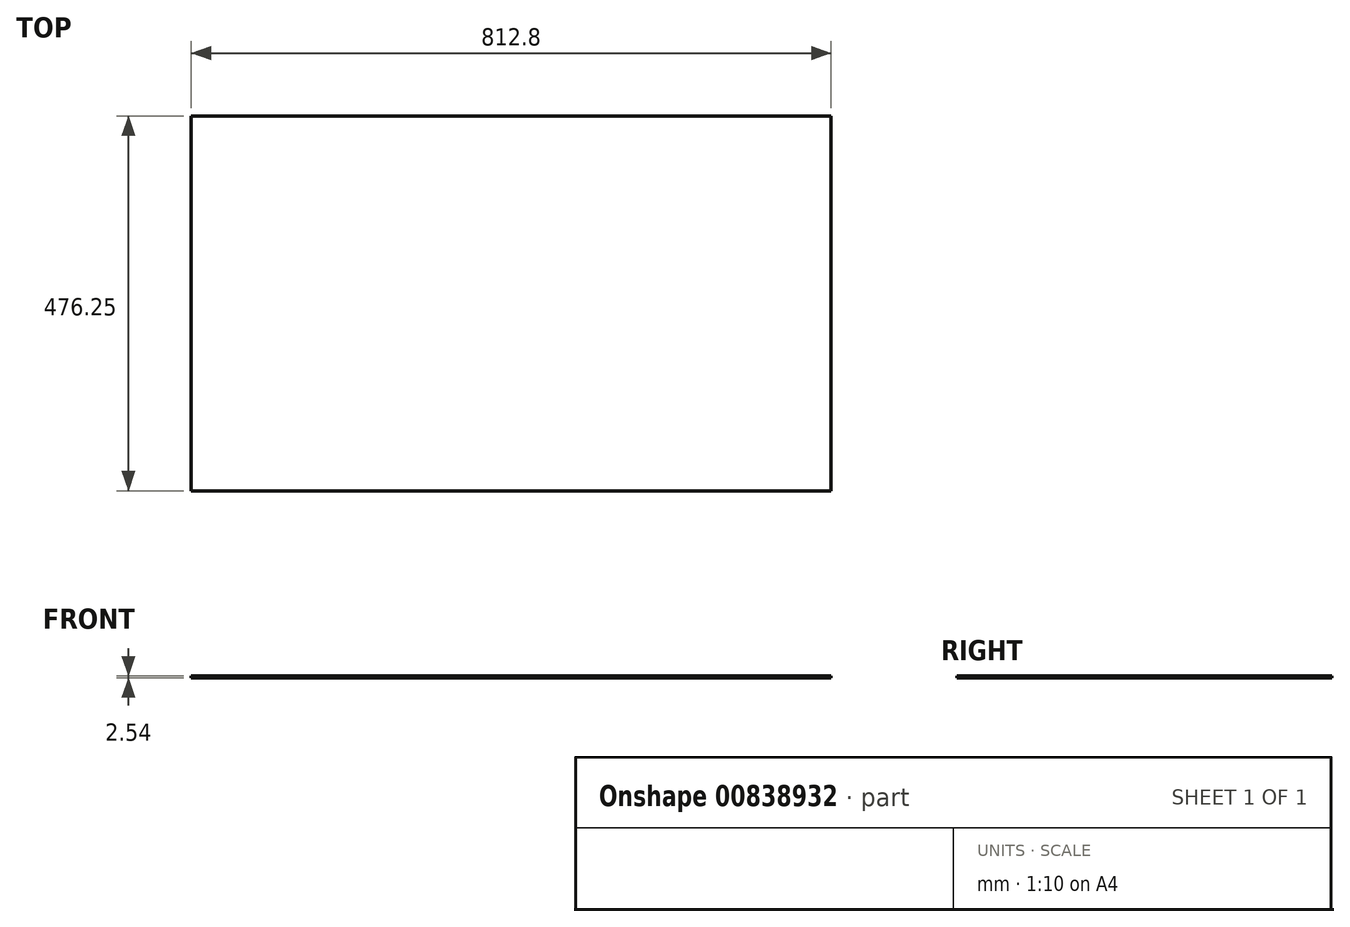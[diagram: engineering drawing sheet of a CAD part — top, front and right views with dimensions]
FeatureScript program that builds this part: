
annotation { "Feature Type Name" : "Feature", "Feature Type Description" : "" }
export const myFeature = defineFeature(function(context is Context, id is Id, definition is map)
    precondition{}
    {
        {
            var Q0;
            Q0=qCreatedBy(makeId("Top.planeOp"),FACE);
            var sketch = newSketch(context, id + "F0", { "sketchPlane" : qUnion([Q0])});
            skLineSegment(sketch, "E0", {"start": v(0, 0) * mm, "end": v(0, 476.25) * mm});
            skLineSegment(sketch, "E1", {"start": v(0, 476.25) * mm, "end": v(812.8, 476.25) * mm});
            skLineSegment(sketch, "E2", {"start": v(812.8, 476.25) * mm, "end": v(812.8, 0) * mm});
            skLineSegment(sketch, "E3", {"start": v(812.8, 0) * mm, "end": v(0, 0) * mm});
            skSolve(sketch);
        }
        {
            var Q0;
            Q0 = qSketchRegion(id + "F0", true);
            extrude(context, id + "F1", {"entities" : qUnion([Q0]), "depth" : 2.54 * mm, "offsetDistance" : 25.4 * mm});
        }
    });
